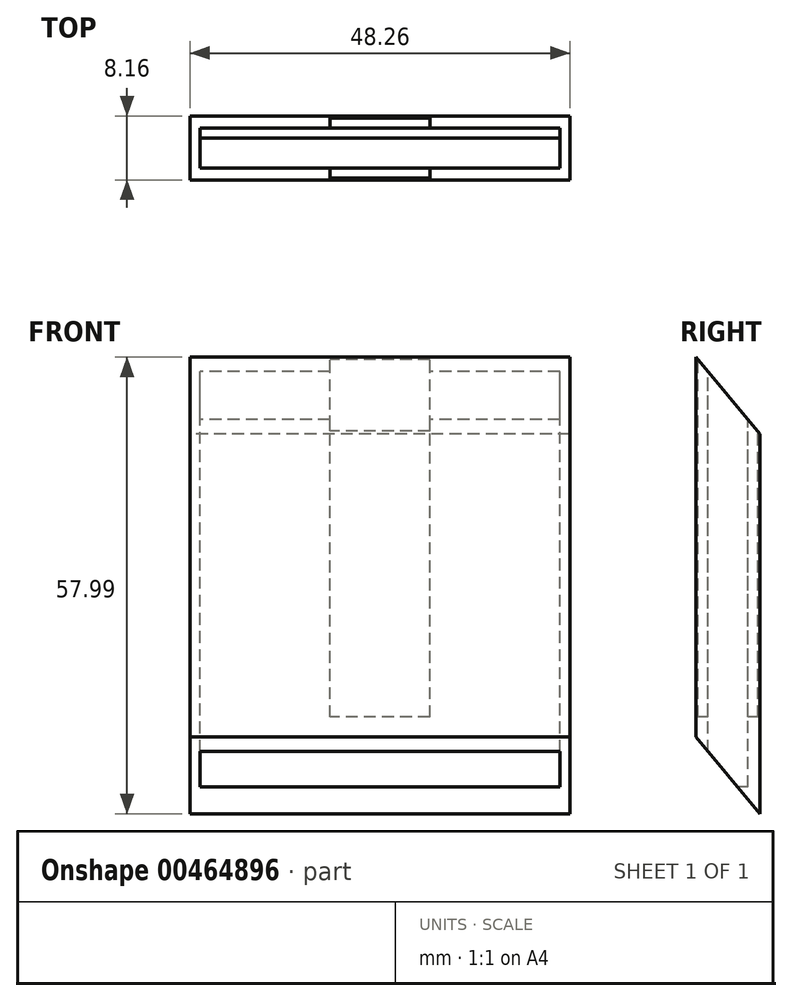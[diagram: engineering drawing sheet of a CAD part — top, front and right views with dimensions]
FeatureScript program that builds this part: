
annotation { "Feature Type Name" : "Feature", "Feature Type Description" : "" }
export const myFeature = defineFeature(function(context is Context, id is Id, definition is map)
    precondition{}
    {
        {
            var Q0;
            Q0=qCreatedBy(makeId("Right.planeOp"),FACE);
            var sketch = newSketch(context, id + "F0", { "sketchPlane" : qUnion([Q0])});
            skLineSegment(sketch, "E0", {"start": v(-24.83, 0) * mm, "end": v(-16.67, -9.73) * mm});
            skLineSegment(sketch, "E1", {"start": v(-24.83, 0) * mm, "end": v(-24.83, -48.26) * mm});
            skLineSegment(sketch, "E2", {"start": v(-24.83, -48.26) * mm, "end": v(-16.67, -57.99) * mm});
            skLineSegment(sketch, "E3", {"start": v(-16.67, -57.99) * mm, "end": v(-16.67, -9.73) * mm});
            skPoint(sketch, "E4.end.orphan", {"position": v(-16.67, -33.86) * mm});
            skPoint(sketch, "E4.start.orphan", {"position": v(-24.83, -24.13) * mm});
            skSolve(sketch);
        }
        {
            var Q0;
            Q0=makeQuery(id+"F0.imprint","IMPRINT",FACE,{"disambiguationData":[TD([[makeQuery(id+"F0.imprint","IMPRINT",EDGE,{"derivedFrom":sQuery(id+"F0.wireOp",EDGE,"E0")}),-1.0]])]});
            extrude(context, id + "F1", {"entities" : qUnion([Q0]), "endBound" : BoundingType.SYMMETRIC, "depth" : 48.26 * mm});
        }
        {
            var Q0;
            Q0=qCreatedBy(makeId("Top.planeOp"),FACE);
            var sketch = newSketch(context, id + "F2", { "sketchPlane" : qUnion([Q0])});
            skLineSegment(sketch, "E5.bottom", {"start": v(22.86, -18.21) * mm, "end": v(-22.86, -18.21) * mm});
            skLineSegment(sketch, "E5.top", {"start": v(22.86, -23.3) * mm, "end": v(-22.86, -23.3) * mm});
            skLineSegment(sketch, "E5.left", {"start": v(22.86, -18.21) * mm, "end": v(22.86, -23.3) * mm});
            skLineSegment(sketch, "E5.right", {"start": v(-22.86, -18.21) * mm, "end": v(-22.86, -23.3) * mm});
            skPoint(sketch, "E5.middle", {"position": v(0, -20.75) * mm});
            skLineSegment(sketch, "E6.bottom", {"start": v(6.35, -16.94) * mm, "end": v(-6.35, -16.94) * mm});
            skLineSegment(sketch, "E6.top", {"start": v(6.35, -24.56) * mm, "end": v(-6.35, -24.56) * mm});
            skLineSegment(sketch, "E6.left", {"start": v(6.35, -16.94) * mm, "end": v(6.35, -18.21) * mm});
            skLineSegment(sketch, "E6.right", {"start": v(-6.35, -16.94) * mm, "end": v(-6.35, -18.21) * mm});
            skPoint(sketch, "E7.orphan", {"position": v(-24.13, -20.75) * mm});
            skLineSegment(sketch, "E8.trimOffspring", {"start": v(-6.35, -23.3) * mm, "end": v(-6.35, -24.56) * mm});
            skLineSegment(sketch, "E9.trimOffspring", {"start": v(6.35, -23.3) * mm, "end": v(6.35, -24.56) * mm});
            skPoint(sketch, "E10.end.orphan", {"position": v(24.13, -20.75) * mm});
            skPoint(sketch, "E11.start.orphan", {"position": v(0, -16.67) * mm});
            skPoint(sketch, "E12.trimOffspring.end.orphan", {"position": v(0, -24.83) * mm});
            skSolve(sketch);
        }
        {
            var Q0;
            Q0=makeQuery(id+"F2.imprint","IMPRINT",FACE,{"disambiguationData":[TD([[makeQuery(id+"F2.imprint","IMPRINT",EDGE,{"derivedFrom":sQuery(id+"F2.wireOp",EDGE,"E6.bottom")}),1.0]])]});
            var Q1;
            Q1=makeQuery(id+"F2.imprint","IMPRINT",FACE,{"disambiguationData":[TD([[makeQuery(id+"F2.imprint","IMPRINT",EDGE,{"derivedFrom":sQuery(id+"F2.wireOp",EDGE,"E6.top")}),-1.0]])]});
            extrude(context, id + "F3", {"entities" : qUnion([Q0, Q1]), "operationType" : NewBodyOperationType.REMOVE, "oppositeDirection" : true, "depth" : 45.72 * mm});
        }
        {
            var Q0;
            {var subQ0=sQuery(id+"F2.wireOp",EDGE,"E5.left");Q0=makeQuery(id+"F2.imprint","IMPRINT",FACE,{"disambiguationData":[TD([[makeQuery(id+"F2.imprint","IMPRINT",EDGE,{"derivedFrom":subQ0}),-1.0]])]});}
            extrude(context, id + "F4", {"entities" : qUnion([Q0]), "operationType" : NewBodyOperationType.REMOVE, "oppositeDirection" : true, "depth" : 54.6 * mm});
        }
    });
